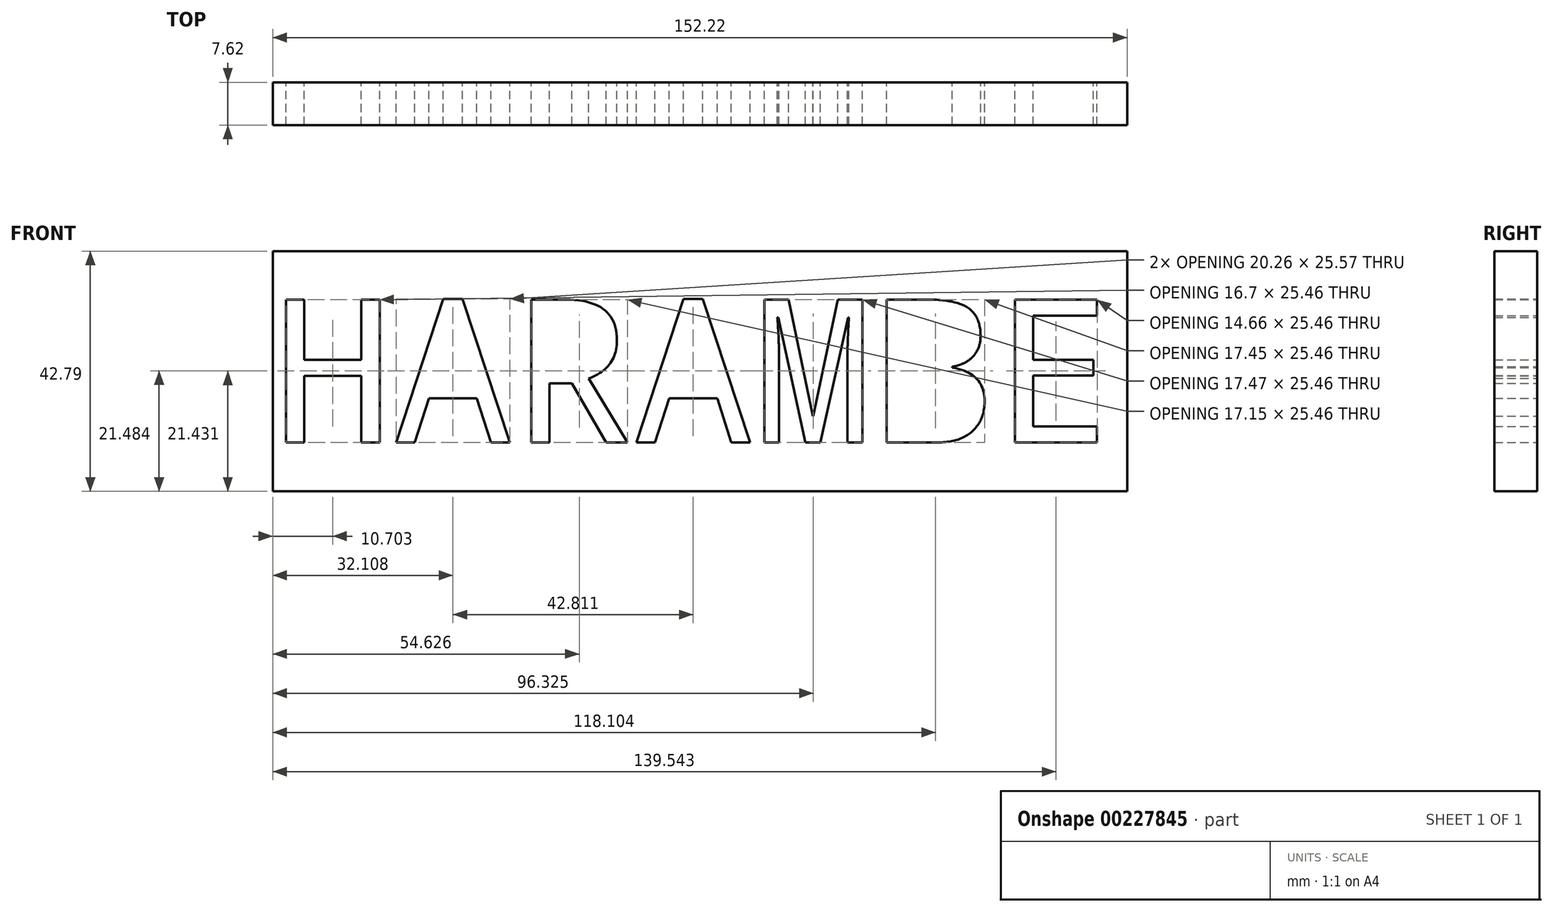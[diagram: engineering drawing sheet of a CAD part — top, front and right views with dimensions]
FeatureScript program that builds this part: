
annotation { "Feature Type Name" : "Feature", "Feature Type Description" : "" }
export const myFeature = defineFeature(function(context is Context, id is Id, definition is map)
    precondition{}
    {
        {
            var Q0;
            Q0=qCreatedBy(makeId("Front.planeOp"),FACE);
            var sketch = newSketch(context, id + "F0", { "sketchPlane" : qUnion([Q0])});
            skLineSegment(sketch, "E0.bottom", {"start": v(-76.25, 42.8) * mm, "end": v(75.97, 42.8) * mm});
            skLineSegment(sketch, "E0.top", {"start": v(-76.25, 0) * mm, "end": v(75.97, 0) * mm});
            skLineSegment(sketch, "E0.left", {"start": v(-76.25, 42.8) * mm, "end": v(-76.25, 0) * mm});
            skLineSegment(sketch, "E0.right", {"start": v(75.97, 42.8) * mm, "end": v(75.97, 0) * mm});
            skText(sketch, "E1", { "text": "HARAMBE", "fontName": "DroidSansMono.ttf"});
            const initialGuessF0  = {"E1": [-0.07625, 0.0087, 1, 0, 0.02568]};
            skSetInitialGuess(sketch, initialGuessF0);
            skSolve(sketch);
        }
        {
            var Q0;
            Q0=makeQuery(id+"F0.imprint","IMPRINT",FACE,{"disambiguationData":[TD([[makeQuery(id+"F0.imprint","IMPRINT",EDGE,{"derivedFrom":sQuery(id+"F0.wireOp",EDGE,"E0.bottom")}),-1.0]])]});
            extrude(context, id + "F1", {"entities" : qUnion([Q0]), "depth" : 7.62 * mm});
        }
    });
